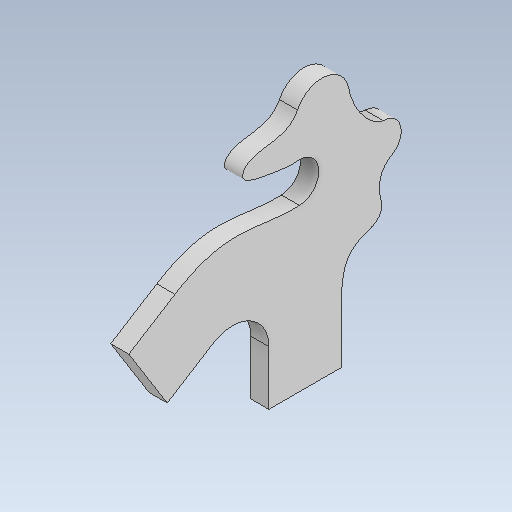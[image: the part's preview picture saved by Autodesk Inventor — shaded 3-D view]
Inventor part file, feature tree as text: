
AUTODESK INVENTOR PART (.ipt)
format: ipt  version: 2021 (Build 250183000, 183)  size: 146,432 bytes
history: native  units: mm
features: other x1, extrude x1, sketch x1
ambient origin geometry x8: Origin, YZ Plane, XZ Plane, XY Plane, X Axis, Y Axis, Z Axis, Center Point
bodies: Body1 (feature_tree)
feature tree (3):
  other  "Sólido1"
  extrude  "Extrusión1"  Depth=5.0mm TaperAngle=0.0deg
  sketch  "Boceto1"  dims[d0=20.0mm d1=60.0deg d2=15.0mm d3=11.0mm d4=15.0mm d5=10.0mm d6=8.0mm d7=0.349066mm d8=50.0mm d9=5.0mm d10=0.0mm]
